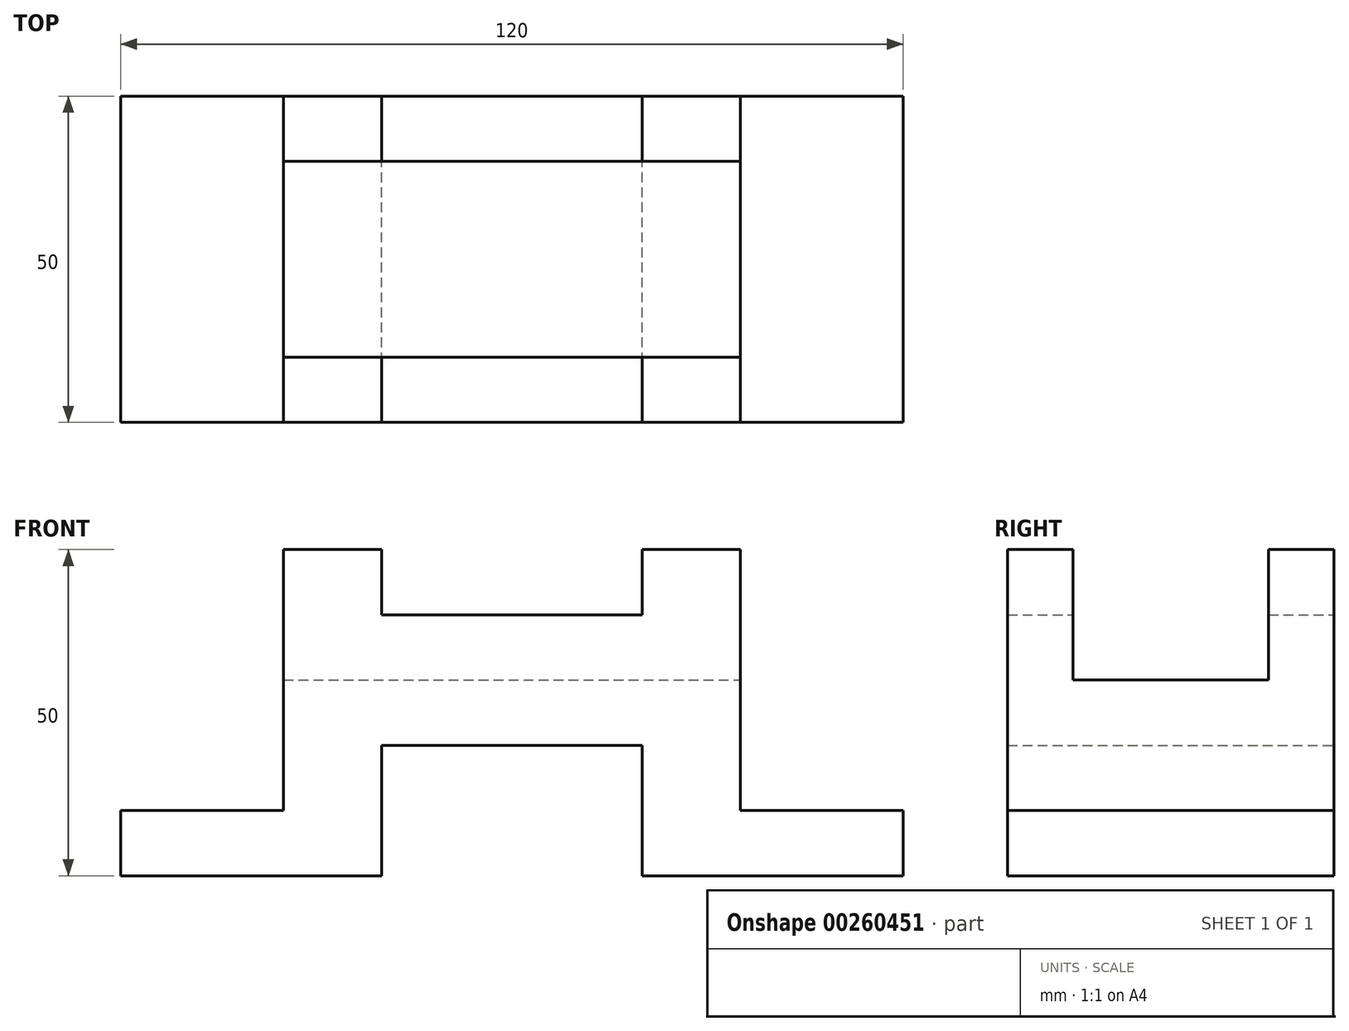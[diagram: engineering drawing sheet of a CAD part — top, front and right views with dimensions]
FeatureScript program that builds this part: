
annotation { "Feature Type Name" : "Feature", "Feature Type Description" : "" }
export const myFeature = defineFeature(function(context is Context, id is Id, definition is map)
    precondition{}
    {
        {
            assignVariable(context, id + "F0", {"name" : "A", "anyValue" : 50});
        }
        {
            var Q0;
            Q0=qCreatedBy(makeId("Front.planeOp"),FACE);
            var sketch = newSketch(context, id + "F1", { "sketchPlane" : qUnion([Q0])});
            skLineSegment(sketch, "E0", {"start": v(-23.17, 0) * mm, "end": v(-60, 0) * mm});
            skLineSegment(sketch, "E1", {"start": v(-60, 0) * mm, "end": v(-60, 10) * mm});
            skLineSegment(sketch, "E2", {"start": v(-60, 10) * mm, "end": v(-35, 10) * mm});
            skLineSegment(sketch, "E3", {"start": v(-35, 10) * mm, "end": v(-35, 50) * mm});
            skLineSegment(sketch, "E4", {"start": v(-35, 50) * mm, "end": v(-20, 50) * mm});
            skLineSegment(sketch, "E5", {"start": v(-20, 50) * mm, "end": v(-20, 40) * mm});
            skLineSegment(sketch, "E6", {"start": v(-20, 40) * mm, "end": v(0, 40) * mm});
            skLineSegment(sketch, "E7", {"start": v(0, 40) * mm, "end": v(0, 20) * mm});
            skLineSegment(sketch, "E8", {"start": v(0, 20) * mm, "end": v(-20, 20) * mm});
            skLineSegment(sketch, "E9", {"start": v(-20, 20) * mm, "end": v(-20, 0) * mm});
            skLineSegment(sketch, "E10", {"start": v(-20, 0) * mm, "end": v(-23.17, 0) * mm});
            skLineSegment(sketch, "E11.MirrorCS", {"start": v(20, 0) * mm, "end": v(23.17, 0) * mm});
            skLineSegment(sketch, "E12.MirrorCS", {"start": v(20, 50) * mm, "end": v(20, 40) * mm});
            skLineSegment(sketch, "E13.MirrorCS", {"start": v(60, 0) * mm, "end": v(60, 10) * mm});
            skLineSegment(sketch, "E14.MirrorCS", {"start": v(20, 20) * mm, "end": v(20, 0) * mm});
            skLineSegment(sketch, "E15.MirrorCS", {"start": v(35, 50) * mm, "end": v(20, 50) * mm});
            skLineSegment(sketch, "E16.MirrorCS", {"start": v(35, 10) * mm, "end": v(35, 50) * mm});
            skLineSegment(sketch, "E17.MirrorCS", {"start": v(60, 10) * mm, "end": v(35, 10) * mm});
            skLineSegment(sketch, "E18.MirrorCS", {"start": v(23.17, 0) * mm, "end": v(60, 0) * mm});
            skLineSegment(sketch, "E19.MirrorCS", {"start": v(20, 40) * mm, "end": v(0, 40) * mm});
            skLineSegment(sketch, "E20.MirrorCS", {"start": v(0, 20) * mm, "end": v(20, 20) * mm});
            skSolve(sketch);
        }
        {
            var Q0;
            Q0=makeQuery(id+"F1.imprint","IMPRINT",FACE,{"disambiguationData":[TD([[makeQuery(id+"F1.imprint","IMPRINT",EDGE,{"derivedFrom":sQuery(id+"F1.wireOp",EDGE,"E0")}),-1.0]])]});
            var Q1;
            Q1=makeQuery(id+"F1.imprint","IMPRINT",FACE,{"disambiguationData":[TD([[makeQuery(id+"F1.imprint","IMPRINT",EDGE,{"derivedFrom":sQuery(id+"F1.wireOp",EDGE,"E7")}),1.0]])]});
            extrude(context, id + "F2", {"entities" : qUnion([Q0, Q1]), "depth" : (getVariable(context, 'A')) * mm});
        }
        {
            var Q0;
            Q0=makeQuery(id+"F2.opExtrude","SWEPT_FACE",FACE,{"disambiguationData":[OSD([sQuery(id+"F1.wireOp",EDGE,"E4")])]});
            var sketch = newSketch(context, id + "F3", { "sketchPlane" : qUnion([Q0])});
            skLineSegment(sketch, "E21.bottom", {"start": v(-35, -10) * mm, "end": v(35, -10) * mm});
            skLineSegment(sketch, "E21.top", {"start": v(-35, -40) * mm, "end": v(35, -40) * mm});
            skLineSegment(sketch, "E21.left", {"start": v(-35, -10) * mm, "end": v(-35, -40) * mm});
            skLineSegment(sketch, "E21.right", {"start": v(35, -10) * mm, "end": v(35, -40) * mm});
            skSolve(sketch);
        }
        {
            var Q0;
            Q0 = qSketchRegion(id + "F3", true);
            extrude(context, id + "F4", {"entities" : qUnion([Q0]), "operationType" : NewBodyOperationType.REMOVE, "oppositeDirection" : true, "depth" : 20 * mm});
        }
    });
